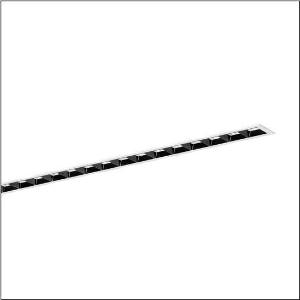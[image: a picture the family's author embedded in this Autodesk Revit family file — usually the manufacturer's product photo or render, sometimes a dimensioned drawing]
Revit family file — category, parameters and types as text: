
# Revit family: silica_r__21_51mx11dc4awb_441a
name_source: partatom
category: Lighting Fixtures
units: mm (PartAtom-declared; Revit-internal decimal feet)

## family parameters
Cut with Voids When Loaded = No
Host = Face
Light Source = No
Part Type = Normal
Room Calculation Point = No
Round Connector Dimension = Use Diameter
Shared = No

## types (1)
- --- (1 x LED, 10800 lm, 64.8 W, 4000K)
    Apparent Load = 65 VA
    CIE Flux Codes = 87 99 100 100 100
    Color Rendering = 80
    Color Temperature = 4000K
    Default Elevation = 1800 mm
    Description = Silica® 21, office luminaire, primary light control with darklight reflector, of PMMA, black, CAT 2 (L<= 3000cd/m²), light emission: direct distribution, primary light characteristic: symmetric, installation type: recessed, LED, rated luminous flux: 10.800lm, luminous efficacy: 167lm/W, light colour: 840, colour temperature: 4000K, with terminal, 3+2-pole, max. 2.5mm², mains connection: 220..240V, AC, 50/60Hz, rated input power: 64.8W, luminaire housing, of aluminium, traffic white (RAL 9016), length: 3.028mm, width: 79mm, height: 53mm, protection rating (complete): IP20, insulation class (complete): insulation class I (protective earthing), certification: CE, permissible operating ambient temperature: 0..+35°C, standard: EN 50419, packaging unit: 1 piece
    Height = 0 mm  [stored 0 ft]
    Lamp = 1 x LED
    Lamp Light Flux = 10800 lm
    Lamp Power = 64.8 W
    Lamp count = 1
    Length = 3027 mm
    Luminous efficacy = 167 lm/W
    Manufacturer = Siteco
    ModVariant = No
    Model = 51MX11DC4AWB
    Mounting Place = Ceiling
    Mounting Type = Recessed
    Number of Poles = 1
    OnlyDefault = Yes
    Power Factor = 1
    Product Name = Silica® 21
    Product group = office luminaire | ceiling recessed
    ProductGroupID = 401
    Protection Class = Protection class I
    Protection Degree = IP 20
    RLX_Detail_Level = 1
    RLX_Emergency_Light_Flux = 0 lm
    RLX_Emergency_Type = 0
    RLX_Emergency_Type_DB = No
    RlxData = <blob elided: 62081 chars, md5=264d4b2e>
    Socket = socket
    Standby Power = 0 W
    System Light Flux = 10800 lm
    System Power = 65 W
    Type Comments = factory setting: luminous flux: 100 % | dim-lin: 254 | 367 mA
    Type Image = l_1313610.jpg
    URL = http://relux.com
    VarID = @adj_072223
    Voltage = 0 V
    Weight = 0.00 kg
    Width = 79 mm

note: [stored X ft] marks values corroborated as IEEE doubles in the binary element streams (Revit-internal decimal feet)

## geometry (parser evidence)
native form markers: Blend x4, Sweep x12
no freeform markers — native parametric forms only
